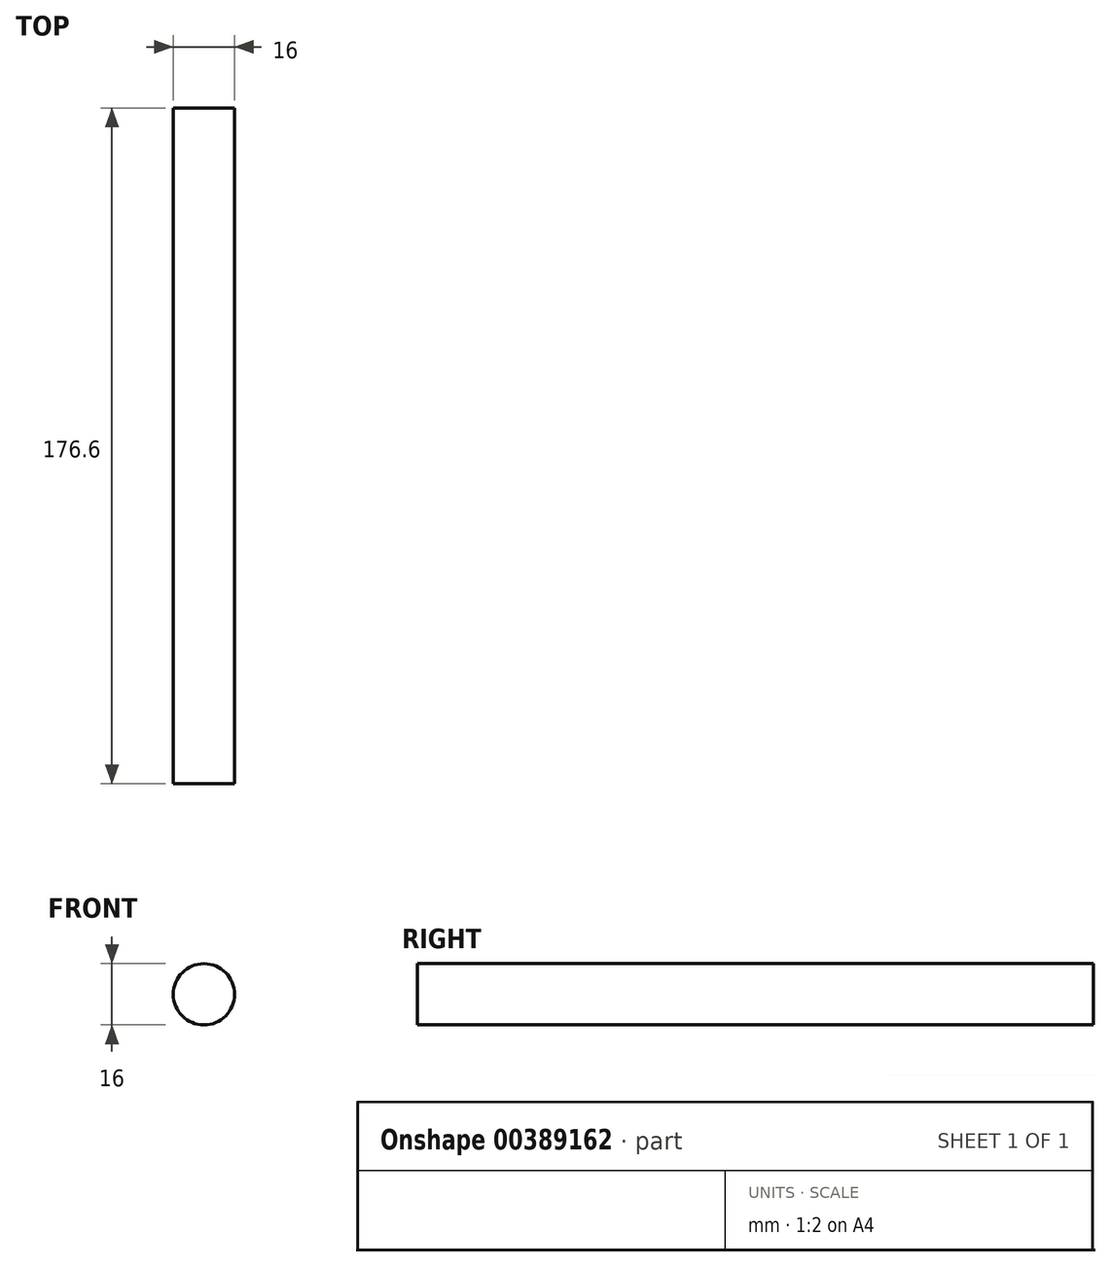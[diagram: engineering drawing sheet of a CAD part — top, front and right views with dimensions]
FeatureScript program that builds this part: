
annotation { "Feature Type Name" : "Feature", "Feature Type Description" : "" }
export const myFeature = defineFeature(function(context is Context, id is Id, definition is map)
    precondition{}
    {
        {
            var Q0;
            Q0=qCreatedBy(makeId("Front.planeOp"),FACE);
            var sketch = newSketch(context, id + "F0", { "sketchPlane" : qUnion([Q0])});
            skCircle(sketch, "E0", {"center": v(0, 0) * mm, "radius": 8 * mm});
            skSolve(sketch);
        }
        {
            var Q0;
            Q0=makeQuery(id+"F0.imprint","IMPRINT",FACE,{"disambiguationData":[TD([[makeQuery(id+"F0.imprint","IMPRINT",EDGE,{"derivedFrom":sQuery(id+"F0.wireOp",EDGE,"E0")}),1.0]])]});
            extrude(context, id + "F1", {"entities" : qUnion([Q0]), "depth" : 150 * mm});
        }
        {
            var Q0;
            Q0=makeQuery(id+"F1.opExtrude","CAP_FACE",FACE,{"disambiguationData":[OSD([sQuery(id+"F0.wireOp",EDGE,"E0")])],"isStart":false});
            extrude(context, id + "F2", {"entities" : qUnion([Q0]), "operationType" : NewBodyOperationType.ADD, "depth" : 26.6 * mm, "offsetDistance" : 25 * mm});
        }
    });
